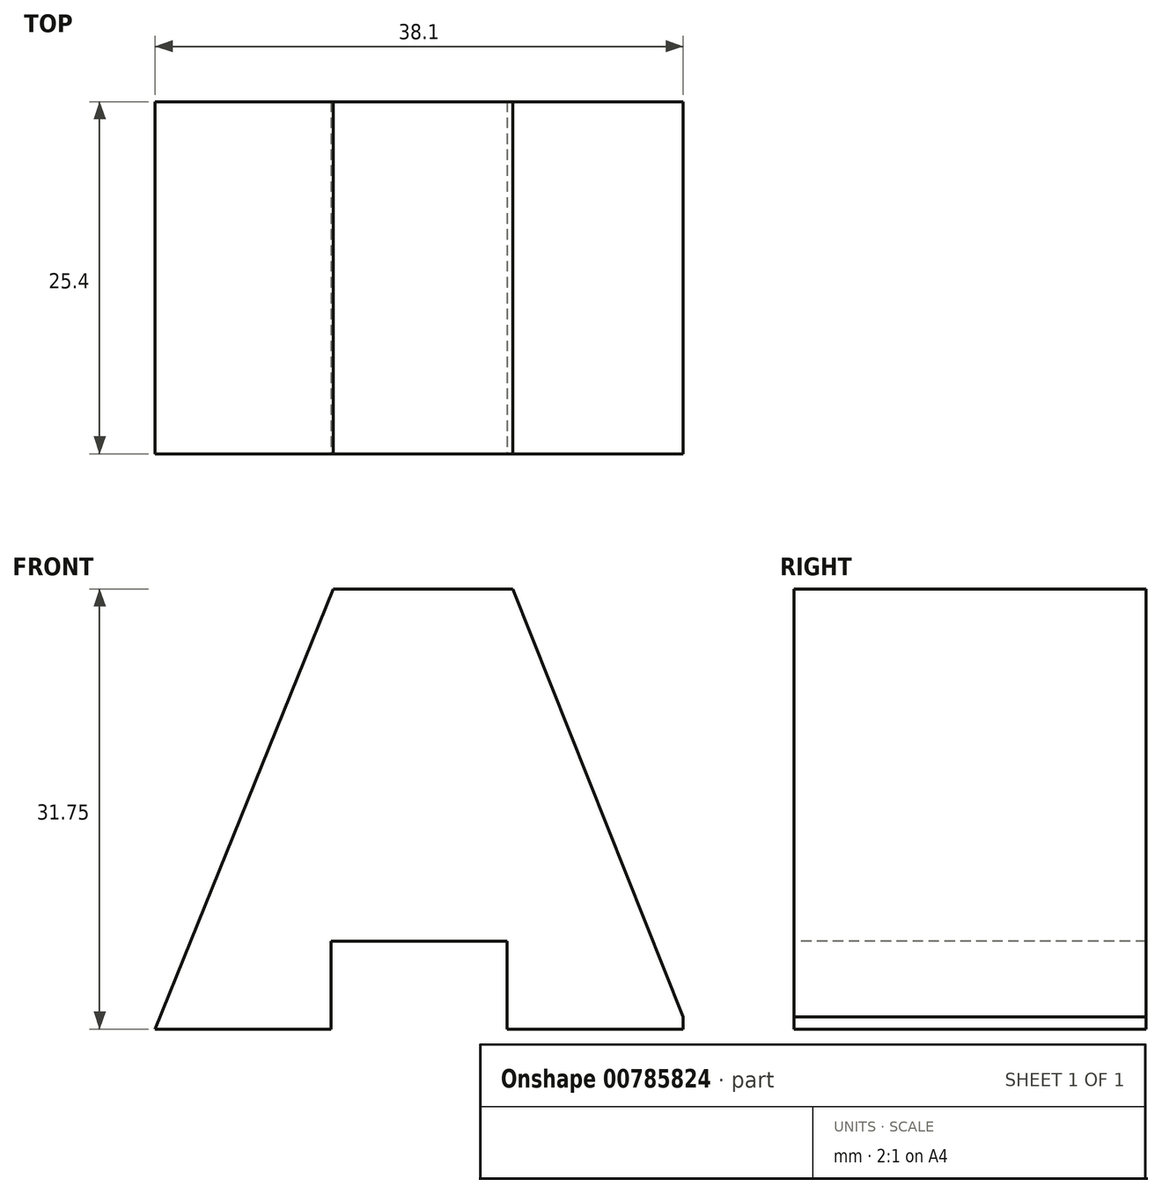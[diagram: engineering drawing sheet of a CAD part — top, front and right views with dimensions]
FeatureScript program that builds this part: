
annotation { "Feature Type Name" : "Feature", "Feature Type Description" : "" }
export const myFeature = defineFeature(function(context is Context, id is Id, definition is map)
    precondition{}
    {
        {
            var Q0;
            Q0=qCreatedBy(makeId("Front.planeOp"),FACE);
            var sketch = newSketch(context, id + "F0", { "sketchPlane" : qUnion([Q0])});
            skLineSegment(sketch, "E0", {"start": v(0, 0) * mm, "end": v(38.1, 0) * mm});
            skLineSegment(sketch, "E1", {"start": v(0, 0) * mm, "end": v(0, 31.75) * mm});
            skLineSegment(sketch, "E2", {"start": v(38.1, 0) * mm, "end": v(38.1, 31.75) * mm});
            skLineSegment(sketch, "E3", {"start": v(0, 31.75) * mm, "end": v(38.1, 31.75) * mm});
            skSolve(sketch);
        }
        {
            var Q0;
            Q0 = qSketchRegion(id + "F0", true);
            extrude(context, id + "F1", {"entities" : qUnion([Q0]), "depth" : 25.4 * mm, "offsetDistance" : 25.4 * mm});
        }
        {
            var Q0;
            Q0=makeQuery(id+"F1.opExtrude","CAP_FACE",FACE,{"disambiguationData":[OSD([sQuery(id+"F0.wireOp",EDGE,"E0"),sQuery(id+"F0.wireOp",EDGE,"E1"),sQuery(id+"F0.wireOp",EDGE,"E2"),sQuery(id+"F0.wireOp",EDGE,"E3")])],"isStart":false});
            var sketch = newSketch(context, id + "F2", { "sketchPlane" : qUnion([Q0])});
            skLineSegment(sketch, "E4", {"start": v(0, 0) * mm, "end": v(12.7, 0) * mm});
            skLineSegment(sketch, "E5", {"start": v(38.1, 0) * mm, "end": v(25.4, 0) * mm});
            skLineSegment(sketch, "E6", {"start": v(12.7, 0) * mm, "end": v(12.7, 6.35) * mm});
            skLineSegment(sketch, "E7", {"start": v(25.4, 0) * mm, "end": v(25.4, 6.35) * mm});
            skLineSegment(sketch, "E8", {"start": v(12.7, 6.35) * mm, "end": v(25.4, 6.35) * mm});
            skLineSegment(sketch, "E9", {"start": v(12.7, 0) * mm, "end": v(0, 0) * mm});
            skSolve(sketch);
        }
        {
            var Q0;
            Q0=makeQuery(id+"F1.opExtrude","CAP_FACE",FACE,{"disambiguationData":[OSD([sQuery(id+"F0.wireOp",EDGE,"E0"),sQuery(id+"F0.wireOp",EDGE,"E1"),sQuery(id+"F0.wireOp",EDGE,"E2"),sQuery(id+"F0.wireOp",EDGE,"E3")])],"isStart":true});
            var sketch = newSketch(context, id + "F3", { "sketchPlane" : qUnion([Q0])});
            skLineSegment(sketch, "E10", {"start": v(-38.1, 0) * mm, "end": v(-25.1, 0) * mm});
            skLineSegment(sketch, "E11", {"start": v(-25.1, 0) * mm, "end": v(-25.1, 6.35) * mm});
            skLineSegment(sketch, "E12", {"start": v(-25.1, 6.35) * mm, "end": v(-12.4, 6.35) * mm});
            skLineSegment(sketch, "E13", {"start": v(-12.4, 6.35) * mm, "end": v(-12.4, 0) * mm});
            skLineSegment(sketch, "E14", {"start": v(-12.4, 0) * mm, "end": v(0, 0) * mm});
            skSolve(sketch);
        }
        {
            var Q0;
            Q0=makeQuery(id+"F3.imprint","IMPRINT",FACE,{"disambiguationData":[TD([[makeQuery(id+"F3.imprint","IMPRINT",EDGE,{"derivedFrom":sQuery(id+"F3.wireOp",EDGE,"E10")}),-1.0]])]});
            var sketch = newSketch(context, id + "F4", { "sketchPlane" : qUnion([Q0])});
            skLineSegment(sketch, "E15", {"start": v(0, 0) * mm, "end": v(-12.63, 32.49) * mm});
            skLineSegment(sketch, "E16", {"start": v(-25.4, 32.77) * mm, "end": v(-38.44, 0) * mm});
            skSolve(sketch);
        }
        {
            var Q0;
            {var subQ0=sQuery(id+"F4.wireOp",EDGE,"E16");var subQ1=makeQuery(id+"F3.imprint","IMPRINT",EDGE,{"derivedFrom":makeQuery(id+"F1.opExtrude","CAP_EDGE",EDGE,{"disambiguationData":[OSD([sQuery(id+"F0.wireOp",EDGE,"E2")])],"isStart":true})});var subQ2=makeQuery(id+"F4.imprint","INTERSECT",VERTEX,{"derivedFrom":[subQ1,subQ0]});Q0=makeQuery(id+"F4.imprint","IMPRINT",FACE,{"disambiguationData":[TD([[makeQuery(id+"F4.imprint","IMPRINT",EDGE,{"disambiguationData":[TD([[subQ2,1.0]])],"derivedFrom":subQ0}),-1.0]])]});}
            extrude(context, id + "F5", {"entities" : qUnion([Q0]), "operationType" : NewBodyOperationType.REMOVE, "oppositeDirection" : true, "depth" : 25.4 * mm, "offsetDistance" : 25.4 * mm});
        }
        {
            var Q0;
            Q0=makeQuery(id+"F3.imprint","IMPRINT",FACE,{"disambiguationData":[TD([[makeQuery(id+"F3.imprint","IMPRINT",EDGE,{"derivedFrom":sQuery(id+"F3.wireOp",EDGE,"E10")}),-1.0]])]});
            var sketch = newSketch(context, id + "F6", { "sketchPlane" : qUnion([Q0])});
            skLineSegment(sketch, "E17", {"start": v(0, 0) * mm, "end": v(-12.9, 31.92) * mm});
            skSolve(sketch);
        }
        {
            var Q0;
            {var subQ1=makeQuery(id+"F3.imprint","IMPRINT",EDGE,{"derivedFrom":makeQuery(id+"F1.opExtrude","CAP_EDGE",EDGE,{"disambiguationData":[OSD([sQuery(id+"F0.wireOp",EDGE,"E1")])],"isStart":true})});Q0=makeQuery(id+"F6.imprint","IMPRINT",FACE,{"disambiguationData":[TD([[makeQuery(id+"F6.imprint","IMPRINT",EDGE,{"derivedFrom":subQ1}),1.0]])]});}
            extrude(context, id + "F7", {"entities" : qUnion([Q0]), "operationType" : NewBodyOperationType.REMOVE, "oppositeDirection" : true, "depth" : 25.4 * mm, "offsetDistance" : 25.4 * mm});
        }
        {
            var Q0;
            {var subQ0=sQuery(id+"F2.wireOp",EDGE,"E6");Q0=makeQuery(id+"F2.imprint","IMPRINT",FACE,{"disambiguationData":[TD([[makeQuery(id+"F2.imprint","IMPRINT",EDGE,{"derivedFrom":subQ0}),-1.0]])]});}
            extrude(context, id + "F8", {"entities" : qUnion([Q0]), "operationType" : NewBodyOperationType.REMOVE, "oppositeDirection" : true, "depth" : 25.4 * mm, "offsetDistance" : 25.4 * mm});
        }
    });
